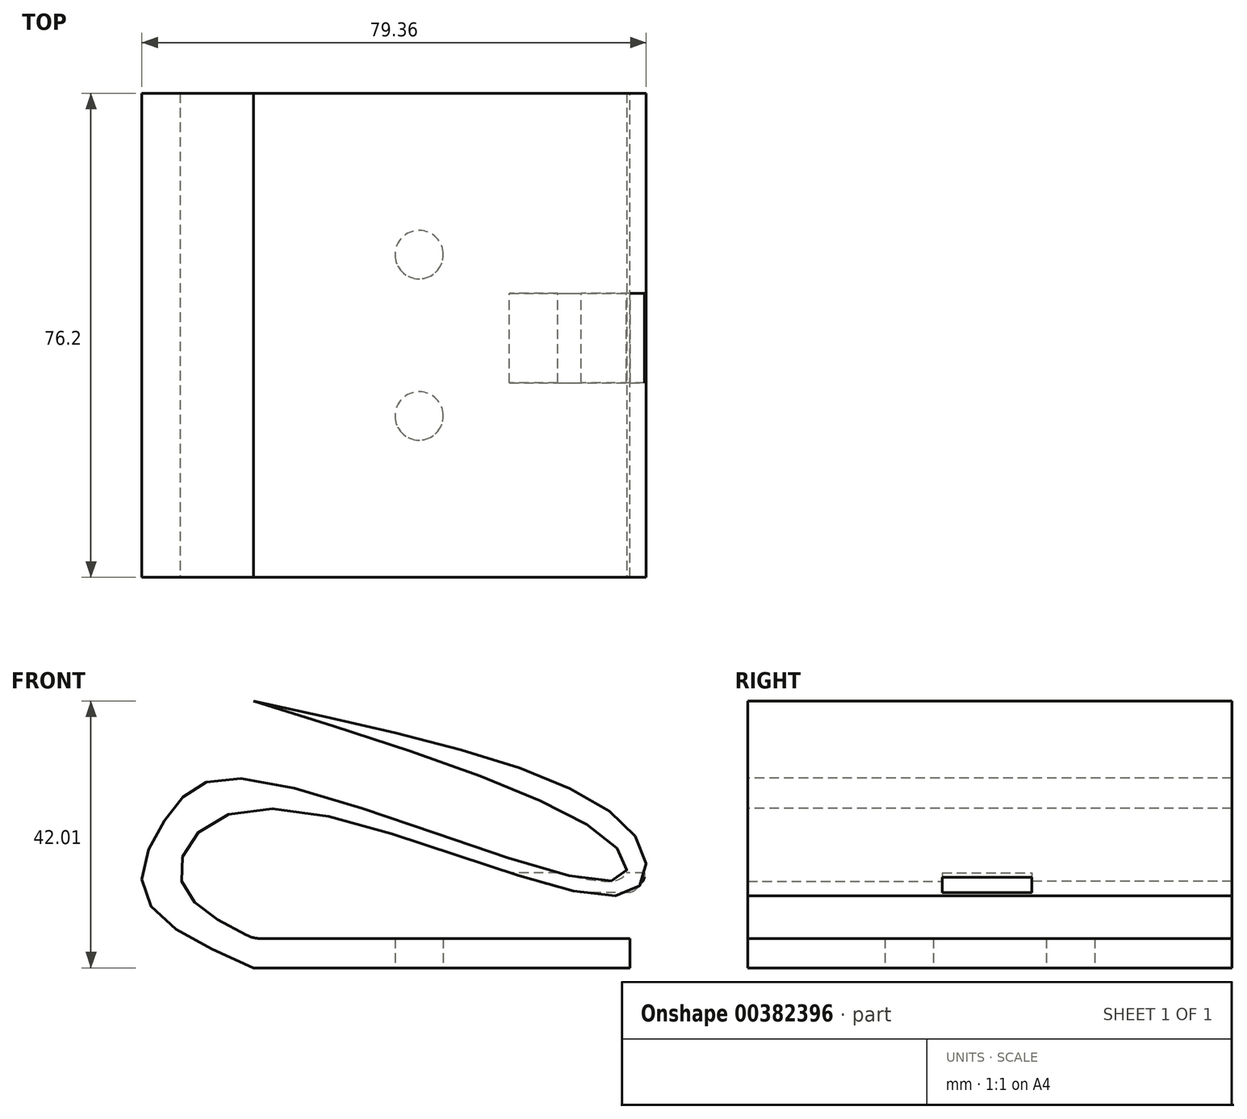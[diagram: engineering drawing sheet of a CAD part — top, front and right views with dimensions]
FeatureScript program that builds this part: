
annotation { "Feature Type Name" : "Feature", "Feature Type Description" : "" }
export const myFeature = defineFeature(function(context is Context, id is Id, definition is map)
    precondition{}
    {
        {
            var Q0;
            Q0=qCreatedBy(makeId("Front.planeOp"),FACE);
            var sketch = newSketch(context, id + "F0", { "sketchPlane" : qUnion([Q0])});
            skLineSegment(sketch, "E0", {"start": v(-36.18, 11.3) * mm, "end": v(23.07, 11.3) * mm});
            skFitSpline(sketch, "E1", {"points": [v(-36.18, 11.3) * mm, v(-47.6, 20.76) * mm, v(-36.18, 31.69) * mm, v(22.58, 18.33) * mm, v(23.8, 27.56) * mm, v(-36.18, 48.69) * mm], "startDerivative": vector(-109.86, 55.2) * mm, "endDerivative": vector(-265, 56.8) * mm});
            skLineSegment(sketch, "E2", {"start": v(23.07, 11.3) * mm, "end": v(23.07, 6.68) * mm});
            skLineSegment(sketch, "E3", {"start": v(23.07, 6.68) * mm, "end": v(-36.18, 6.68) * mm});
            skFitSpline(sketch, "E4", {"points": [v(-36.18, 6.68) * mm, v(-53.42, 18.58) * mm, v(-49.05, 31.45) * mm, v(-36.18, 36.3) * mm, v(21.13, 20.52) * mm, v(21.37, 25.13) * mm, v(-36.18, 48.69) * mm], "startDerivative": vector(-152.8, 66.61) * mm, "endDerivative": vector(-291.71, 91) * mm});
            skSolve(sketch);
        }
        {
            var Q0;
            Q0 = qSketchRegion(id + "F0", true);
            extrude(context, id + "F1", {"entities" : qUnion([Q0]), "depth" : 76.2 * mm});
        }
        {
            var Q0;
            Q0=makeQuery(id+"F1.opExtrude","SWEPT_EDGE",EDGE,{"disambiguationData":[OSD([sQuery(id+"F0.wireOp",EDGE,"E0"),sQuery(id+"F0.wireOp",EDGE,"E1")])]});
            fillet(context, id + "F2", {"entities" : qUnion([Q0]), "radius" : 5.08 * mm, "tangentPropagation" : true, "allowEdgeOverflow" : false});
        }
        {
            var Q0;
            Q0=makeQuery(id+"F1.opExtrude","SWEPT_FACE",FACE,{"disambiguationData":[OSD([sQuery(id+"F0.wireOp",EDGE,"E3")])]});
            var sketch = newSketch(context, id + "F3", { "sketchPlane" : qUnion([Q0])});
            skCircle(sketch, "E5", {"center": v(-10.09, 25.4) * mm, "radius": 3.81 * mm});
            skCircle(sketch, "E6", {"center": v(-10.09, 50.8) * mm, "radius": 3.81 * mm});
            skSolve(sketch);
        }
        {
            var Q0;
            Q0 = qSketchRegion(id + "F3", true);
            extrude(context, id + "F4", {"entities" : qUnion([Q0]), "operationType" : NewBodyOperationType.REMOVE, "endBound" : BoundingType.UP_TO_NEXT, "oppositeDirection" : true, "depth" : 25.4 * mm});
        }
        {
            var Q0;
            Q0=qCreatedBy(makeId("Right.planeOp"),FACE);
            var sketch = newSketch(context, id + "F5", { "sketchPlane" : qUnion([Q0])});
            skLineSegment(sketch, "E7.bottom", {"start": v(-45.58, 21.67) * mm, "end": v(-31.5, 21.67) * mm});
            skLineSegment(sketch, "E7.top", {"start": v(-45.58, 18.53) * mm, "end": v(-31.5, 18.53) * mm});
            skLineSegment(sketch, "E7.left", {"start": v(-45.58, 21.67) * mm, "end": v(-45.58, 18.53) * mm});
            skLineSegment(sketch, "E7.right", {"start": v(-31.5, 21.67) * mm, "end": v(-31.5, 18.53) * mm});
            skSolve(sketch);
        }
        {
            var Q0;
            Q0 = qSketchRegion(id + "F5", true);
            extrude(context, id + "F6", {"entities" : qUnion([Q0]), "operationType" : NewBodyOperationType.REMOVE, "depth" : 25.4 * mm});
        }
    });
